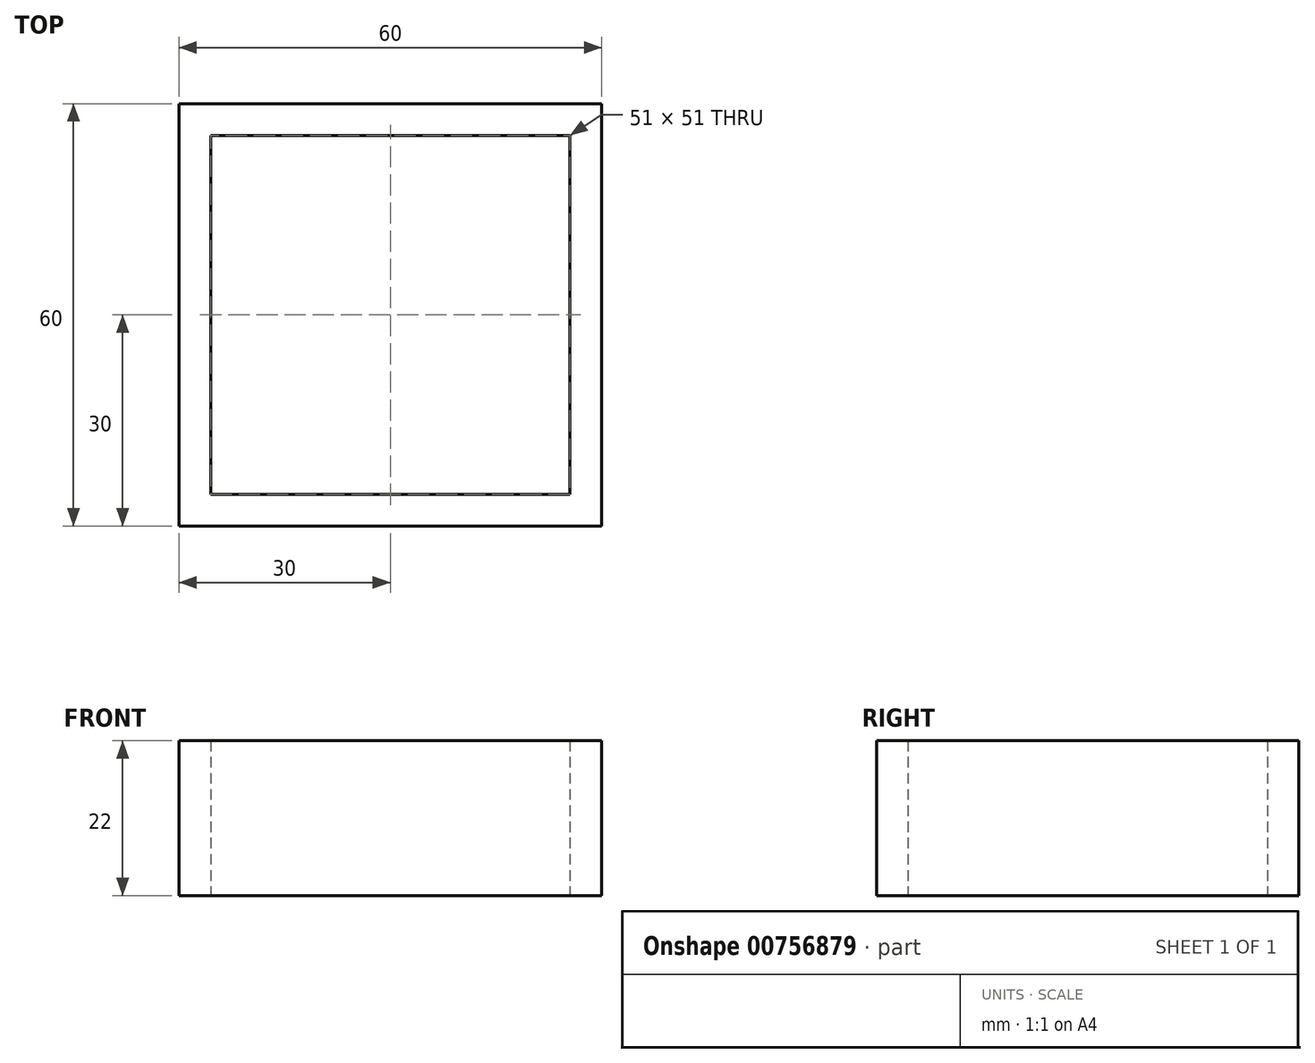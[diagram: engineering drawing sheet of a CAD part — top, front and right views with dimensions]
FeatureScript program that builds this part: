
annotation { "Feature Type Name" : "Feature", "Feature Type Description" : "" }
export const myFeature = defineFeature(function(context is Context, id is Id, definition is map)
    precondition{}
    {
        {
            var Q0;
            Q0=qCreatedBy(makeId("Top.planeOp"),FACE);
            var sketch = newSketch(context, id + "F0", { "sketchPlane" : qUnion([Q0])});
            skLineSegment(sketch, "E0.bottom", {"start": v(25.5, -25.5) * mm, "end": v(-25.5, -25.5) * mm});
            skLineSegment(sketch, "E0.top", {"start": v(25.5, 25.5) * mm, "end": v(-25.5, 25.5) * mm});
            skLineSegment(sketch, "E0.left", {"start": v(25.5, -25.5) * mm, "end": v(25.5, 25.5) * mm});
            skLineSegment(sketch, "E0.right", {"start": v(-25.5, -25.5) * mm, "end": v(-25.5, 25.5) * mm});
            skPoint(sketch, "E0.middle", {"position": v(0, 0) * mm});
            skLineSegment(sketch, "E1.bottom", {"start": v(30, -30) * mm, "end": v(-30, -30) * mm});
            skLineSegment(sketch, "E1.top", {"start": v(30, 30) * mm, "end": v(-30, 30) * mm});
            skLineSegment(sketch, "E1.left", {"start": v(30, -30) * mm, "end": v(30, 30) * mm});
            skLineSegment(sketch, "E1.right", {"start": v(-30, -30) * mm, "end": v(-30, 30) * mm});
            skSolve(sketch);
        }
        {
            var Q0;
            Q0=makeQuery(id+"F0.imprint","IMPRINT",FACE,{"disambiguationData":[TD([[makeQuery(id+"F0.imprint","IMPRINT",EDGE,{"derivedFrom":sQuery(id+"F0.wireOp",EDGE,"E0.bottom")}),1.0]])]});
            extrude(context, id + "F1", {"entities" : qUnion([Q0]), "depth" : 22 * mm, "offsetDistance" : 25 * mm});
        }
    });
